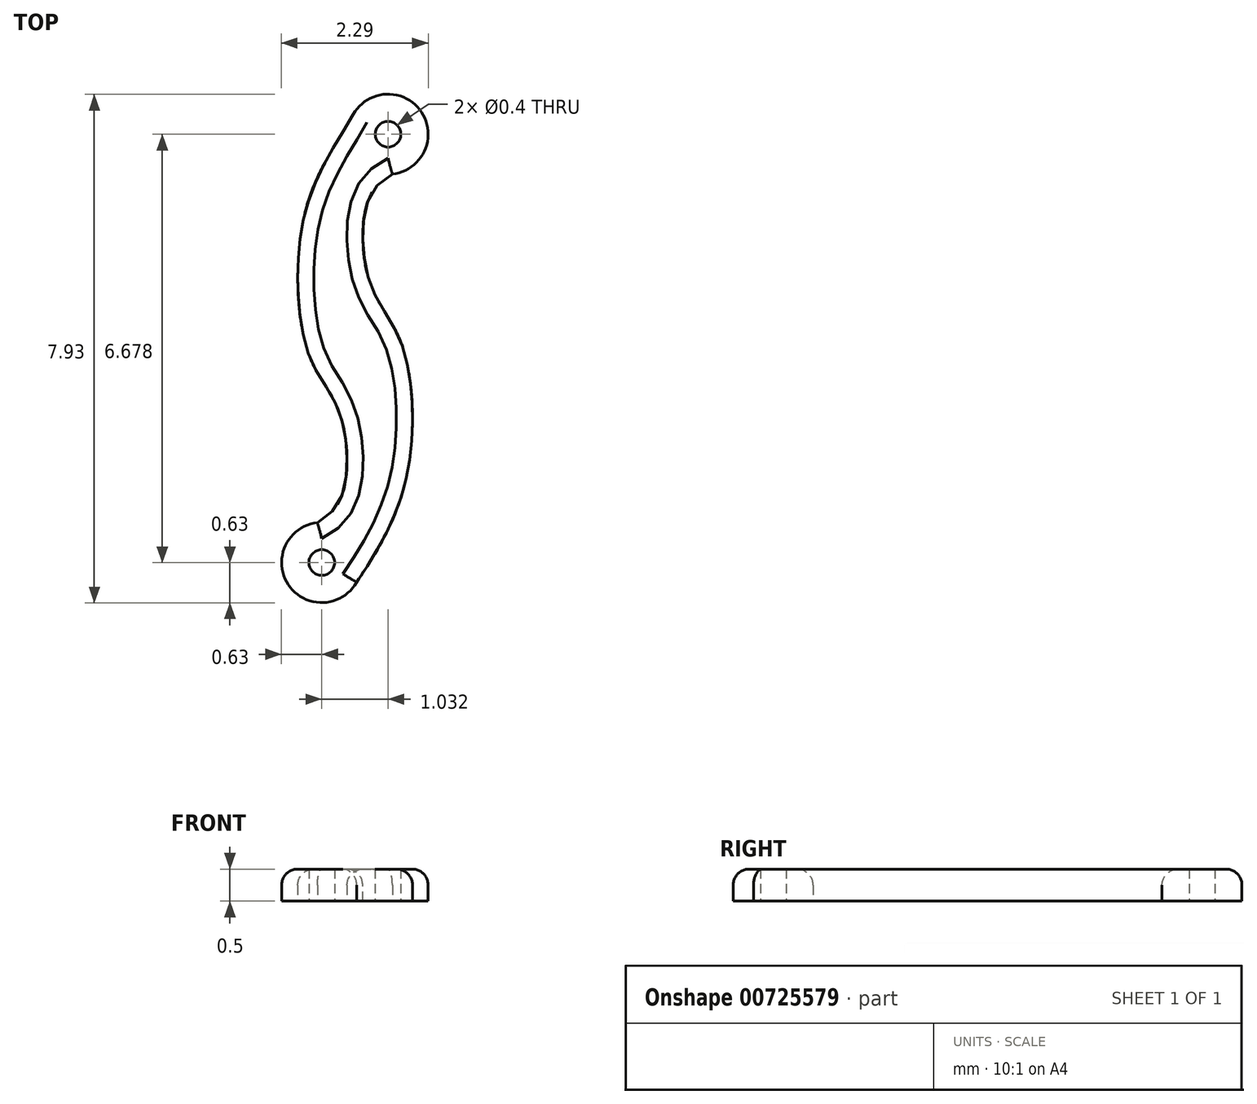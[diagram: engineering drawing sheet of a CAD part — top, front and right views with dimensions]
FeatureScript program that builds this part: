
annotation { "Feature Type Name" : "Feature", "Feature Type Description" : "" }
export const myFeature = defineFeature(function(context is Context, id is Id, definition is map)
    precondition{}
    {
        {
            var Q0;
            Q0=qCreatedBy(makeId("Top.planeOp"),FACE);
            var sketch = newSketch(context, id + "F0", { "sketchPlane" : qUnion([Q0])});
            skCircle(sketch, "E0", {"center": v(0, 0) * mm, "radius": 0.2 * mm});
            skCircle(sketch, "E1", {"center": v(1.03, 6.68) * mm, "radius": 0.2 * mm});
            skCircle(sketch, "E2", {"center": v(1.03, 6.68) * mm, "radius": 0.62 * mm});
            skCircle(sketch, "E3", {"center": v(0, 0) * mm, "radius": 0.62 * mm});
            skFitSpline(sketch, "E4", {"points": [v(0.54, -0.3) * mm, v(1.3, 1.22) * mm, v(1.24, 3.4) * mm, v(0.76, 4.33) * mm, v(0.7, 5.6) * mm, v(1.1, 6.06) * mm], "startDerivative": vector(3.34, 5.08) * mm, "endDerivative": vector(3.75, 1.9) * mm});
            skLineSegment(sketch, "E5", {"start": v(0, 0) * mm, "end": v(1.03, 6.68) * mm, "construction": true});
            skFitSpline(sketch, "E6", {"points": [v(-0.07, 0.62) * mm, v(0.32, 1.07) * mm, v(0.27, 2.35) * mm, v(-0.21, 3.27) * mm, v(-0.26, 5.46) * mm, v(0.49, 6.99) * mm, v(1.87, 8.73) * mm], "startDerivative": vector(4.73, 2.4) * mm, "endDerivative": vector(9.73, 4.4) * mm});
            skSolve(sketch);
        }
        {
            var Q0;
            Q0=makeQuery(id+"F0.imprint","IMPRINT",FACE,{"disambiguationData":[TD([[makeQuery(id+"F0.imprint","IMPRINT",EDGE,{"derivedFrom":sQuery(id+"F0.wireOp",EDGE,"E0")}),-1.0]])]});
            var Q1;
            {var subQ0=sQuery(id+"F0.wireOp",EDGE,"E4");Q1=makeQuery(id+"F0.imprint","IMPRINT",FACE,{"disambiguationData":[TD([[makeQuery(id+"F0.imprint","IMPRINT",EDGE,{"derivedFrom":subQ0}),1.0]])]});}
            var Q2;
            Q2=makeQuery(id+"F0.imprint","IMPRINT",FACE,{"disambiguationData":[TD([[makeQuery(id+"F0.imprint","IMPRINT",EDGE,{"derivedFrom":sQuery(id+"F0.wireOp",EDGE,"E1")}),-1.0]])]});
            extrude(context, id + "F1", {"entities" : qUnion([Q0, Q1, Q2]), "depth" : .5 * mm, "offsetDistance" : 25 * mm});
        }
        {
            var Q0;
            Q0=makeQuery(id+"F1.opExtrude","CAP_EDGE",EDGE,{"disambiguationData":[OSD([sQuery(id+"F0.wireOp",EDGE,"E4")])],"isStart":false});
            fillet(context, id + "F2", {"entities" : qUnion([Q0]), "radius" : .25 * mm, "tangentPropagation" : true, "allowEdgeOverflow" : false});
        }
        {
            var Q0;
            Q0=makeQuery(id+"F1.opExtrude","CAP_EDGE",EDGE,{"disambiguationData":[OSD([sQuery(id+"F0.wireOp",EDGE,"E6")])],"isStart":false});
            var Q1;
            Q1=makeQuery(id+"F1.opExtrude","CAP_EDGE",EDGE,{"disambiguationData":[OSD([sQuery(id+"F0.wireOp",EDGE,"E3")])],"isStart":false});
            fillet(context, id + "F3", {"entities" : qUnion([Q0, Q1]), "radius" : .25 * mm, "tangentPropagation" : true, "allowEdgeOverflow" : false});
        }
    });
